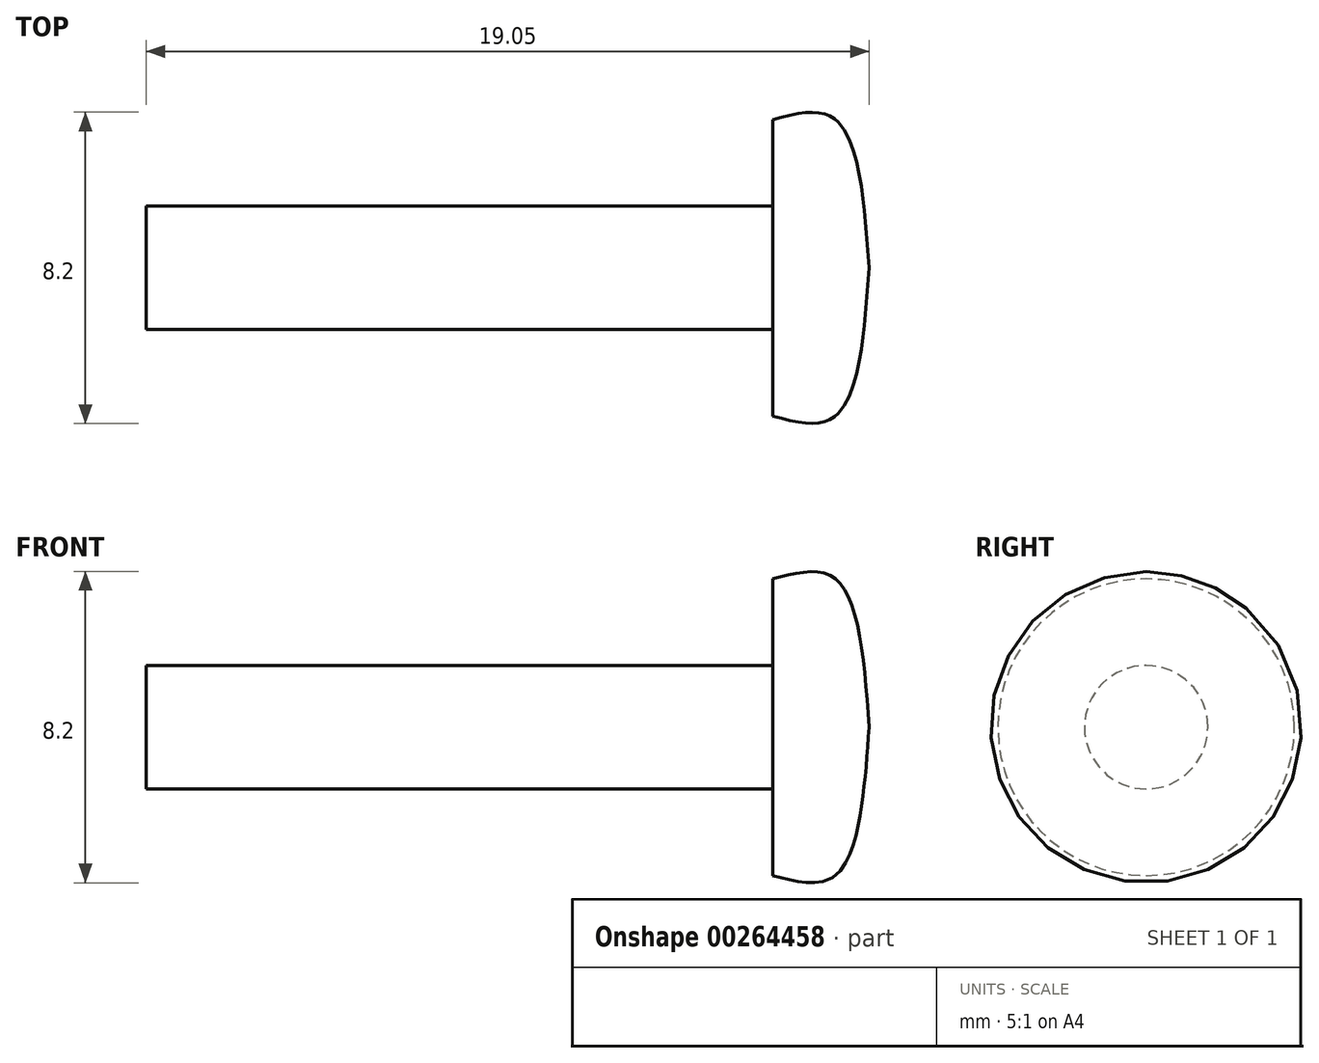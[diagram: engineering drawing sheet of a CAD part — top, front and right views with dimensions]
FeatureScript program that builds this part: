
annotation { "Feature Type Name" : "Feature", "Feature Type Description" : "" }
export const myFeature = defineFeature(function(context is Context, id is Id, definition is map)
    precondition{}
    {
        {
            var Q0;
            Q0=qCreatedBy(makeId("Front.planeOp"),FACE);
            var sketch = newSketch(context, id + "F0", { "sketchPlane" : qUnion([Q0])});
            skLineSegment(sketch, "E0", {"start": v(0, 0) * mm, "end": v(19.05, 0) * mm});
            skLineSegment(sketch, "E1", {"start": v(0, 0) * mm, "end": v(0, 1.63) * mm});
            skLineSegment(sketch, "E2", {"start": v(0, 1.63) * mm, "end": v(16.51, 1.63) * mm});
            skLineSegment(sketch, "E3", {"start": v(16.51, 1.63) * mm, "end": v(16.51, 3.9) * mm});
            skFitSpline(sketch, "E4", {"points": [v(16.51, 3.9) * mm, v(18.16, 3.9) * mm, v(19.05, 0) * mm], "startDerivative": vector(4.77, 1.25) * mm, "endDerivative": vector(0.61, -8.37) * mm});
            skPoint(sketch, "E5.1.internal.orphan", {"position": v(18.06, 1.63) * mm});
            skSolve(sketch);
        }
        {
            var Q0;
            Q0=makeQuery(id+"F0.imprint","IMPRINT",FACE,{"disambiguationData":[TD([[makeQuery(id+"F0.imprint","IMPRINT",EDGE,{"derivedFrom":sQuery(id+"F0.wireOp",EDGE,"E0")}),1.0]])]});
            var Q1;
            Q1=sQuery(id+"F0.wireOp",EDGE,"E0");
            revolve(context, id + "F1", {"entities" : qUnion([Q0]), "axis" : qUnion([Q1]), "revolveType" : RevolveType.FULL});
        }
    });
